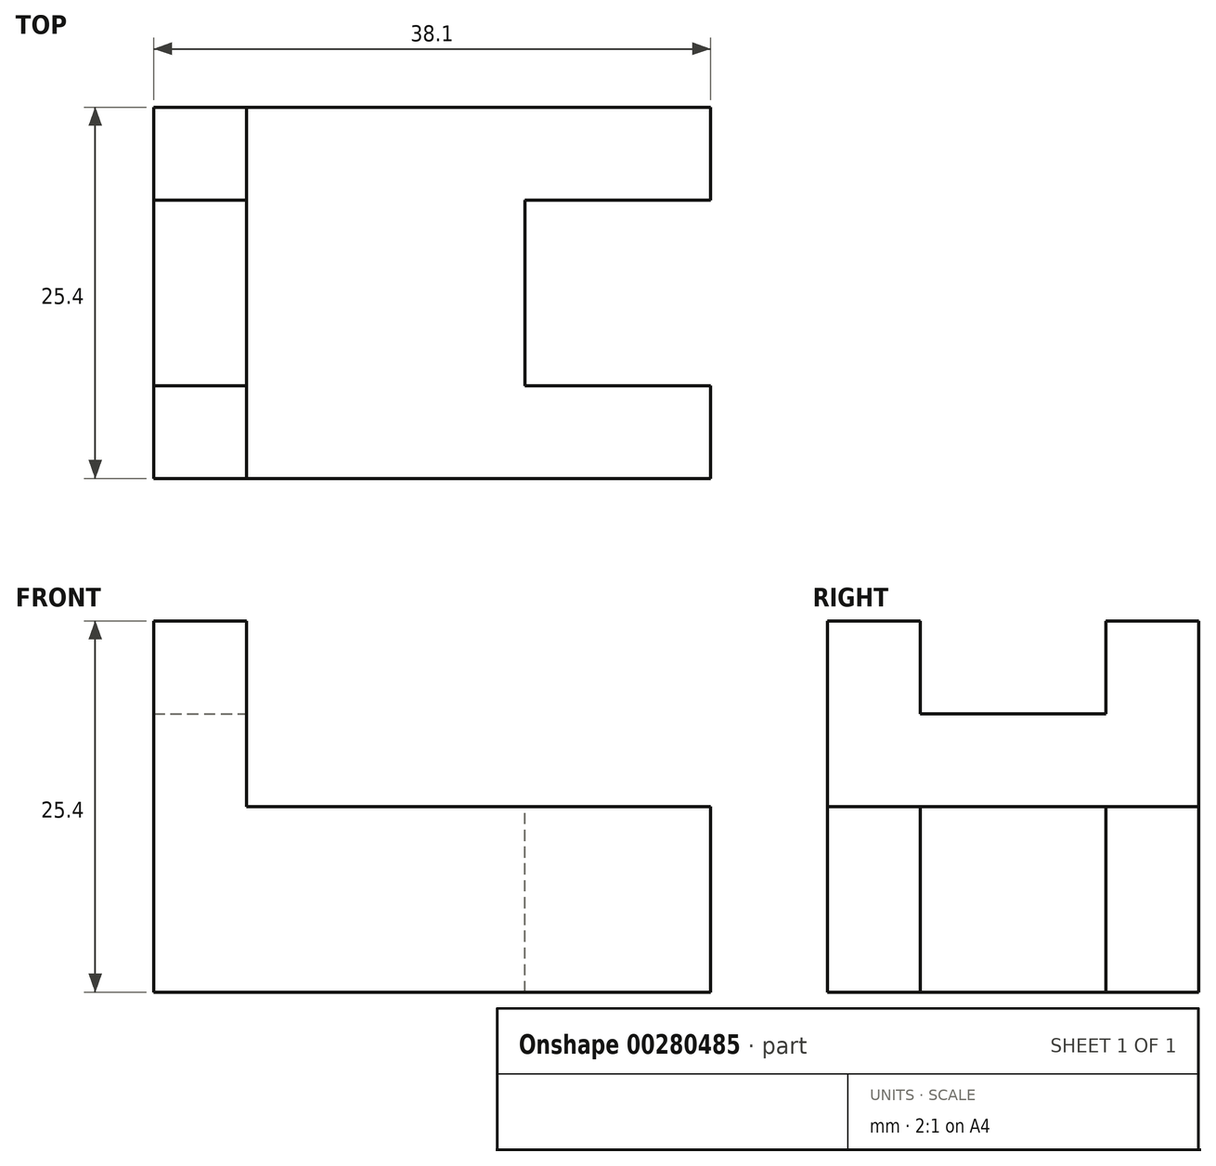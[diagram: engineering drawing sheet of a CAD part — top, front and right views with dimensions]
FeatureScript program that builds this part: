
annotation { "Feature Type Name" : "Feature", "Feature Type Description" : "" }
export const myFeature = defineFeature(function(context is Context, id is Id, definition is map)
    precondition{}
    {
        {
            var Q0;
            Q0=qCreatedBy(makeId("Top.planeOp"),FACE);
            var sketch = newSketch(context, id + "F0", { "sketchPlane" : qUnion([Q0])});
            skLineSegment(sketch, "E0.bottom", {"start": v(0, 0) * mm, "end": v(38.1, 0) * mm});
            skLineSegment(sketch, "E0.top", {"start": v(0, 25.4) * mm, "end": v(38.1, 25.4) * mm});
            skLineSegment(sketch, "E0.left", {"start": v(0, 0) * mm, "end": v(0, 25.4) * mm});
            skLineSegment(sketch, "E0.right", {"start": v(38.1, 0) * mm, "end": v(38.1, 25.4) * mm});
            skSolve(sketch);
        }
        {
            var Q0;
            Q0 = qSketchRegion(id + "F0", true);
            extrude(context, id + "F1", {"entities" : qUnion([Q0]), "oppositeDirection" : true, "depth" : 12.7 * mm});
        }
        {
            var Q0;
            Q0=makeQuery(id+"F1.opExtrude","CAP_FACE",FACE,{"disambiguationData":[OSD([sQuery(id+"F0.wireOp",EDGE,"E0.bottom"),sQuery(id+"F0.wireOp",EDGE,"E0.top"),sQuery(id+"F0.wireOp",EDGE,"E0.left"),sQuery(id+"F0.wireOp",EDGE,"E0.right")])],"isStart":true});
            var sketch = newSketch(context, id + "F2", { "sketchPlane" : qUnion([Q0])});
            skLineSegment(sketch, "E1.bottom", {"start": v(38.1, 6.35) * mm, "end": v(25.4, 6.35) * mm});
            skLineSegment(sketch, "E1.top", {"start": v(38.1, 19.05) * mm, "end": v(25.4, 19.05) * mm});
            skLineSegment(sketch, "E1.left", {"start": v(38.1, 6.35) * mm, "end": v(38.1, 19.05) * mm});
            skLineSegment(sketch, "E1.right", {"start": v(25.4, 6.35) * mm, "end": v(25.4, 19.05) * mm});
            skSolve(sketch);
        }
        {
            var Q0;
            Q0 = qSketchRegion(id + "F2", true);
            extrude(context, id + "F3", {"entities" : qUnion([Q0]), "operationType" : NewBodyOperationType.REMOVE, "endBound" : BoundingType.THROUGH_ALL, "oppositeDirection" : true, "depth" : 25.4 * mm});
        }
        {
            var Q0;
            Q0=makeQuery(id+"F1.opExtrude","CAP_FACE",FACE,{"disambiguationData":[OSD([sQuery(id+"F0.wireOp",EDGE,"E0.bottom"),sQuery(id+"F0.wireOp",EDGE,"E0.top"),sQuery(id+"F0.wireOp",EDGE,"E0.left"),sQuery(id+"F0.wireOp",EDGE,"E0.right")])],"isStart":true});
            var sketch = newSketch(context, id + "F4", { "sketchPlane" : qUnion([Q0])});
            skLineSegment(sketch, "E2.bottom", {"start": v(0, 25.4) * mm, "end": v(6.35, 25.4) * mm});
            skLineSegment(sketch, "E2.top", {"start": v(0, 0) * mm, "end": v(6.35, 0) * mm});
            skLineSegment(sketch, "E2.left", {"start": v(0, 25.4) * mm, "end": v(0, 0) * mm});
            skLineSegment(sketch, "E2.right", {"start": v(6.35, 25.4) * mm, "end": v(6.35, 0) * mm});
            skSolve(sketch);
        }
        {
            var Q0;
            Q0 = qSketchRegion(id + "F4", true);
            extrude(context, id + "F5", {"entities" : qUnion([Q0]), "operationType" : NewBodyOperationType.ADD, "depth" : 12.7 * mm});
        }
        {
            var Q0;
            Q0=makeQuery(id+"F5.opExtrude","CAP_FACE",FACE,{"disambiguationData":[OSD([sQuery(id+"F4.wireOp",EDGE,"E2.bottom"),sQuery(id+"F4.wireOp",EDGE,"E2.top"),sQuery(id+"F4.wireOp",EDGE,"E2.left"),sQuery(id+"F4.wireOp",EDGE,"E2.right")])],"isStart":false});
            var sketch = newSketch(context, id + "F6", { "sketchPlane" : qUnion([Q0])});
            skLineSegment(sketch, "E3.bottom", {"start": v(0, 19.05) * mm, "end": v(6.35, 19.05) * mm});
            skLineSegment(sketch, "E3.top", {"start": v(0, 6.35) * mm, "end": v(6.35, 6.35) * mm});
            skLineSegment(sketch, "E3.left", {"start": v(0, 19.05) * mm, "end": v(0, 6.35) * mm});
            skLineSegment(sketch, "E3.right", {"start": v(6.35, 19.05) * mm, "end": v(6.35, 6.35) * mm});
            skSolve(sketch);
        }
        {
            var Q0;
            Q0 = qSketchRegion(id + "F6", true);
            extrude(context, id + "F7", {"entities" : qUnion([Q0]), "operationType" : NewBodyOperationType.REMOVE, "oppositeDirection" : true, "depth" : 6.35 * mm});
        }
    });
